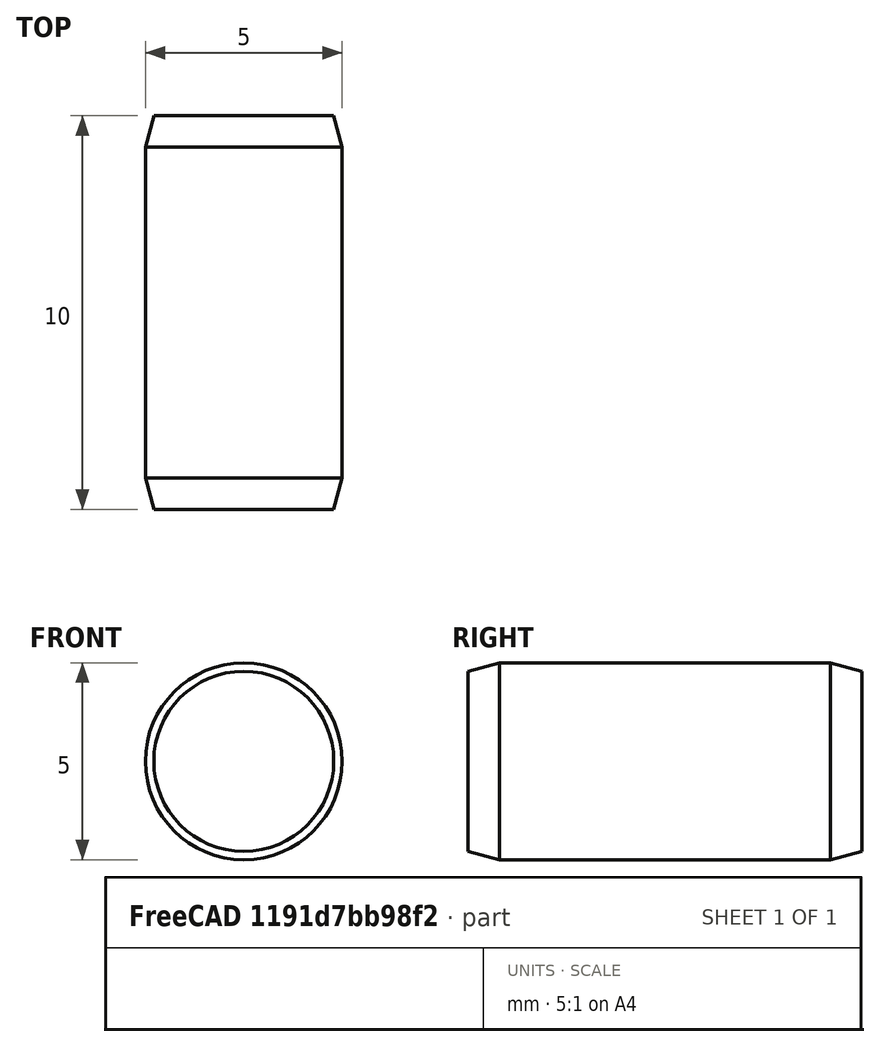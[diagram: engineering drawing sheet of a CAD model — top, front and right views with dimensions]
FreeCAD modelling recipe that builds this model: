
FCSTD DOCUMENT  (FreeCAD 0.15R4470 (Git))
Label: Zyl-Stift_ISO_2338-5x10
License: CC-BY 3.0
LicenseURL: http://creativecommons.org/licenses/by/3.0/
objects: Sketcher::SketchObject×1, PartDesign::Revolution×1
note: 3 computed .brp shape members not serialized (recipe doc carries the construction recipe); baked Part::Feature solids carry a one-line shape summary decoded from their .brp

FEATURE [Sketcher::SketchObject] Sketch
  Placement = pos=(0,0,0) rot=(0.57735,0.57735,0.57735;2.0944rad)
  sketch-geometry (7):
    g0: LineSegment StartX=0 StartY=0 StartZ=0 EndX=0 EndY=2.28564 EndZ=0
    g1: LineSegment StartX=0 StartY=2.28564 StartZ=0 EndX=0.8 EndY=2.5 EndZ=0
    g2: LineSegment StartX=0.8 StartY=2.5 StartZ=0 EndX=9.2 EndY=2.5 EndZ=0
    g3: LineSegment StartX=9.2 StartY=2.5 StartZ=0 EndX=10 EndY=2.28564 EndZ=0
    g4: LineSegment StartX=10 StartY=2.28564 StartZ=0 EndX=10 EndY=0 EndZ=0
    g5: LineSegment StartX=10 StartY=0 StartZ=0 EndX=0 EndY=0 EndZ=0
    g6: LineSegment [constr] StartX=0 StartY=2.28564 StartZ=0 EndX=10 EndY=2.28564 EndZ=0
  constraints (19):
    c: Coincident(g0,g-1)
    c: PointOnObject(g0,g-2)
    c: Coincident(g0,g1)
    c: Coincident(g1,g2)
    c: Horizontal(g2)
    c: Coincident(g2,g3)
    c: Coincident(g3,g4)
    c: Vertical(g4)
    c: Coincident(g4,g5)
    c: Coincident(g5,g-1)
    c: Horizontal(g5)
    c: Equal(g3,g1)
    c: Coincident(g6,g0)
    c: Coincident(g6,g3)
    c: Horizontal(g6)
    c: Angle(g6,g1) = 0.261799
    c: DistanceY(g-1,g1) = 2.5
    c: DistanceX(g5) = -10
    c: DistanceX(g1) = 0.8
FEATURE [PartDesign::Revolution] Revolution  label="Zyl-Stift ISO 2338-5x10 #"
  Angle = 360
  Axis = (0,1,0)
  Base = (0,0,0)
  Placement = pos=(0,0,0) rot=(0.57735,0.57735,0.57735;2.0944rad)
  ReferenceAxis = -> Sketch [H_Axis]
  Sketch = -> Sketch
